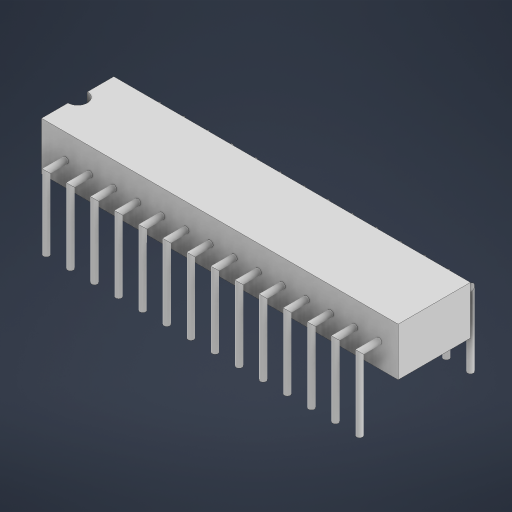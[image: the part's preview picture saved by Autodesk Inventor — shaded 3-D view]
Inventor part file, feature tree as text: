
AUTODESK INVENTOR PART (.ipt)
format: ipt  version: 2024 (Build 280153000, 153)  size: 304,640 bytes
history: native  units: in
note: dims shown in document units (in); Inventor stores cm internally (conversion verified against a paired STEP export)
features: sketch x5, sweep x2, extrude x1
ambient origin geometry x8: Origin, YZ Plane, XZ Plane, XY Plane, X Axis, Y Axis, Z Axis, Center Point
bodies: Solid1 (feature_tree)
feature tree (8):
  extrude  "Extrusion1"  Depth=0.2953in
  sweep  "Sweep1"
  sweep  "Sweep2"
  sketch  "Sketch1"  dims[d0=1.4567in d1=0.2953in]
  sketch  "Sketch2"  dims[d2=0.0787in d3=0.1969in d4=0.0in]
  sketch  "3D Sketch1"
  sketch  "Sketch3"  dims[d5=0.0236in d7=0.0236in d8=0.0236in d9=0.0236in d11=0.0236in d12=0.0236in d13=0.0236in d14=0.0236in d15=0.0236in d16=0.0236in d17=0.0236in d18=0.0236in d19=0.0236in d20=0.0236in d23=0.0787in d24=0.2953in d25=0.0in d26=0.0in d27=0.0787in d28=0.2953in d29=0.0in d30=0.0in]
  sketch  "3D Sketch2"
